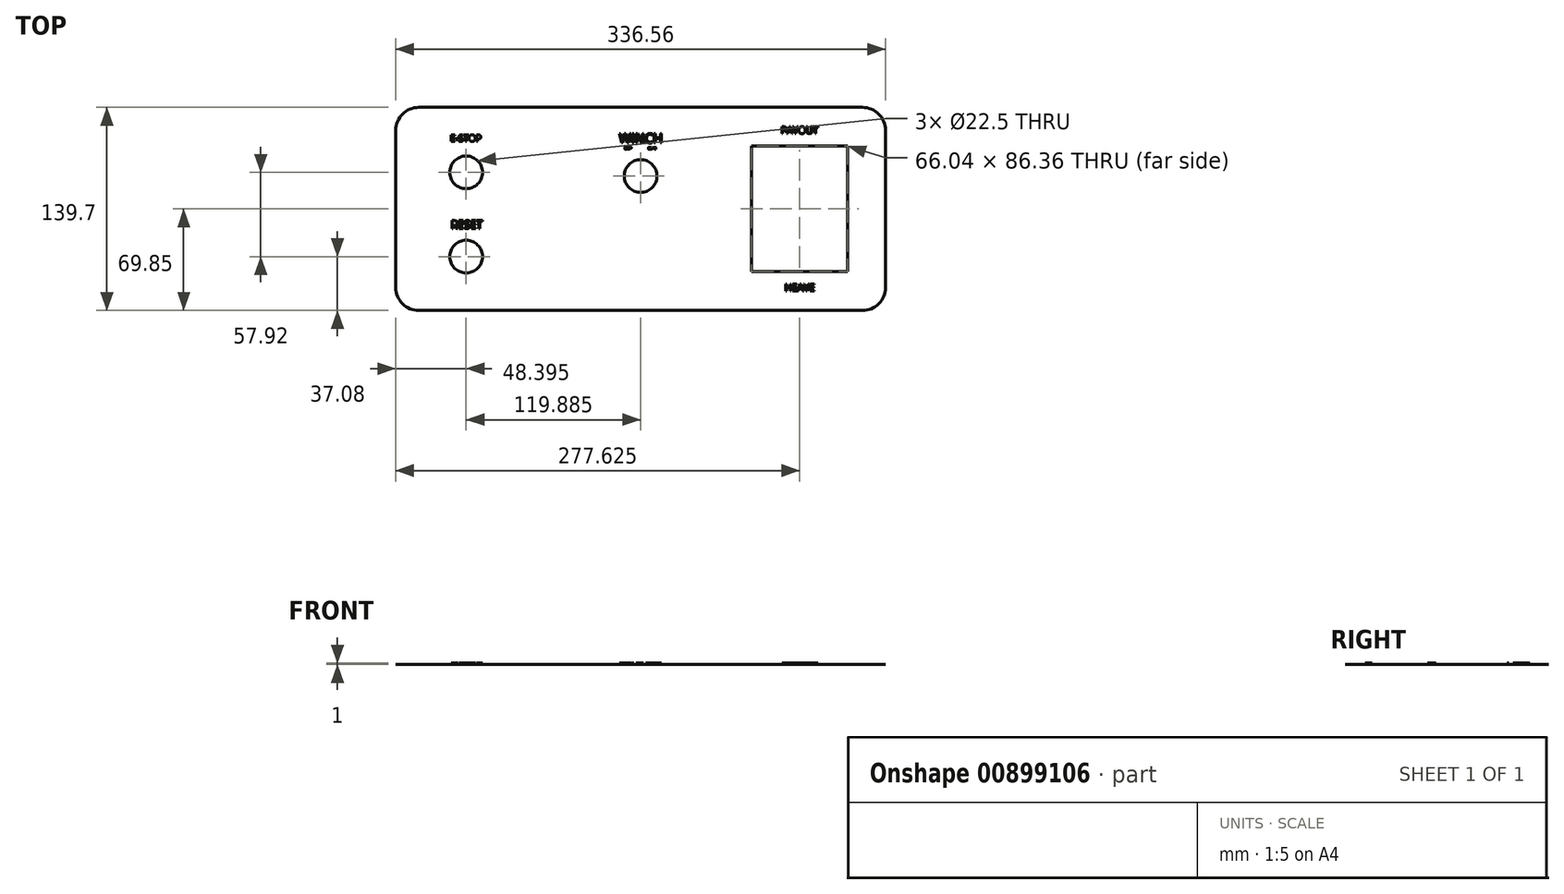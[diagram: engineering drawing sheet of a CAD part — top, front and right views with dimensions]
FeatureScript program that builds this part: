
annotation { "Feature Type Name" : "Feature", "Feature Type Description" : "" }
export const myFeature = defineFeature(function(context is Context, id is Id, definition is map)
    precondition{}
    {
        {
            var Q0;
            Q0=qCreatedBy(makeId("Top.planeOp"),FACE);
            var sketch = newSketch(context, id + "F0", { "sketchPlane" : qUnion([Q0])});
            skLineSegment(sketch, "E0.bottom", {"start": v(168.28, -69.85) * mm, "end": v(-168.28, -69.85) * mm});
            skLineSegment(sketch, "E0.top", {"start": v(168.28, 69.85) * mm, "end": v(-168.28, 69.85) * mm});
            skLineSegment(sketch, "E0.left", {"start": v(168.28, -69.85) * mm, "end": v(168.28, 69.85) * mm});
            skLineSegment(sketch, "E0.right", {"start": v(-168.28, -69.85) * mm, "end": v(-168.28, 69.85) * mm});
            skPoint(sketch, "E0.middle", {"position": v(0, 0) * mm});
            skCircle(sketch, "E1", {"center": v(-119.89, 25.15) * mm, "radius": 11.25 * mm});
            skCircle(sketch, "E2", {"center": v(-119.89, -32.77) * mm, "radius": 11.25 * mm});
            skLineSegment(sketch, "E3.bottom", {"start": v(142.37, -43.18) * mm, "end": v(76.33, -43.18) * mm});
            skLineSegment(sketch, "E3.top", {"start": v(142.37, 43.18) * mm, "end": v(76.33, 43.18) * mm});
            skLineSegment(sketch, "E3.left", {"start": v(142.37, -43.18) * mm, "end": v(142.37, 43.18) * mm});
            skLineSegment(sketch, "E3.right", {"start": v(76.33, -43.18) * mm, "end": v(76.33, 43.18) * mm});
            skPoint(sketch, "E3.middle", {"position": v(109.35, 0) * mm});
            skCircle(sketch, "E4", {"center": v(0, 22.65) * mm, "radius": 11.25 * mm});
            skSolve(sketch);
        }
        {
            var Q0;
            Q0 = qSketchRegion(id + "F0", true);
            extrude(context, id + "F1", {"entities" : qUnion([Q0]), "depth" : 1 * mm, "offsetDistance" : 25 * mm});
        }
        {
            var Q0;
            Q0=makeQuery(id+"F1.opExtrude","SWEPT_EDGE",EDGE,{"disambiguationData":[OSD([sQuery(id+"F0.wireOp",EDGE,"E0.top"),sQuery(id+"F0.wireOp",EDGE,"E0.right")])]});
            var Q1;
            Q1=makeQuery(id+"F1.opExtrude","SWEPT_EDGE",EDGE,{"disambiguationData":[OSD([sQuery(id+"F0.wireOp",EDGE,"E0.bottom"),sQuery(id+"F0.wireOp",EDGE,"E0.right")])]});
            var Q2;
            Q2=makeQuery(id+"F1.opExtrude","SWEPT_EDGE",EDGE,{"disambiguationData":[OSD([sQuery(id+"F0.wireOp",EDGE,"E0.top"),sQuery(id+"F0.wireOp",EDGE,"E0.left")])]});
            var Q3;
            Q3=makeQuery(id+"F1.opExtrude","SWEPT_EDGE",EDGE,{"disambiguationData":[OSD([sQuery(id+"F0.wireOp",EDGE,"E0.bottom"),sQuery(id+"F0.wireOp",EDGE,"E0.left")])]});
            fillet(context, id + "F2", {"entities" : qUnion([Q0, Q1, Q2, Q3]), "radius" : 15.88 * mm, "tangentPropagation" : true, "allowEdgeOverflow" : false});
        }
        {
            var Q0;
            Q0=makeQuery(id+"F1.opExtrude","CAP_FACE",FACE,{"disambiguationData":[OSD([sQuery(id+"F0.wireOp",EDGE,"E0.bottom"),sQuery(id+"F0.wireOp",EDGE,"E0.top"),sQuery(id+"F0.wireOp",EDGE,"E0.left"),sQuery(id+"F0.wireOp",EDGE,"E0.right"),sQuery(id+"F0.wireOp",EDGE,"E1"),sQuery(id+"F0.wireOp",EDGE,"E2"),sQuery(id+"F0.wireOp",EDGE,"Ul4tBXo7-cBAq-A29W-g4Bs-Gp345ctHy5ez"),sQuery(id+"F0.wireOp",EDGE,"E3.bottom"),sQuery(id+"F0.wireOp",EDGE,"E3.top"),sQuery(id+"F0.wireOp",EDGE,"E3.left"),sQuery(id+"F0.wireOp",EDGE,"E3.right")])],"isStart":false});
            var sketch = newSketch(context, id + "F3", { "sketchPlane" : qUnion([Q0])});
            skText(sketch, "E5", { "text": "E-STOP", "fontName": "OpenSans-Regular.ttf"});
            skText(sketch, "E6", { "text": "RESET", "fontName": "OpenSans-Regular.ttf"});
            skText(sketch, "E7", { "text": "WINCH", "fontName": "OpenSans-Regular.ttf"});
            skText(sketch, "E8", { "text": "STOP                       START", "fontName": "OpenSans-Regular.ttf"});
            skText(sketch, "E9", { "text": "PAYOUT", "fontName": "OpenSans-Regular.ttf"});
            skPoint(sketch, "E10", {"position": v(109.35, 43.18) * mm});
            skText(sketch, "E11", { "text": "HEAVE", "fontName": "OpenSans-Regular.ttf"});
            skPoint(sketch, "E12", {"position": v(109.35, -43.18) * mm});
            const initialGuessF3  = {"E5": [-0.13071, 0.04642, 1, 0, 0.00455], "E6": [-0.1304, -0.01345, 1, 0, 0.00555], "E7": [-0.01483, 0.0454, 1, 0, 0.00648], "E8": [-0.01092, 0.04107, 1, 0, 0.00138], "E9": [0.09635, 0.0518, 1, 0, 0.00479], "E11": [0.09894, -0.0564, 1, 0, 0.00486]};
            skSetInitialGuess(sketch, initialGuessF3);
            skSolve(sketch);
        }
        {
            var Q0;
            Q0=makeQuery(id+"F3.imprint","IMPRINT",FACE,{"disambiguationData":[TD([[makeQuery(id+"F3.imprint","IMPRINT",EDGE,{"derivedFrom":sQuery(id+"F3.wireOp",EDGE,"E5.sketch_text.stroke-0")}),1.0]])]});
            extrude(context, id + "F4", {"entities" : qUnion([Q0]), "operationType" : NewBodyOperationType.REMOVE, "oppositeDirection" : true, "depth" : 0.9 * mm, "offsetDistance" : 25 * mm});
        }
    });
